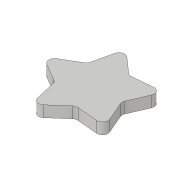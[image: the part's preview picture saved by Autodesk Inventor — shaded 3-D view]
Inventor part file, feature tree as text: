
AUTODESK INVENTOR PART (.ipt)
format: ipt  version: 2019 (Build 230136000, 136)  size: 109,568 bytes
history: native  units: in
note: dims shown in document units (in); Inventor stores cm internally (conversion verified against a paired STEP export)
features: fillet x2, extrude x1, sketch x1
ambient origin geometry x8: Origin, YZ Plane, XZ Plane, XY Plane, X Axis, Y Axis, Z Axis, Center Point
bodies: Body1 (feature_tree)
feature tree (4):
  extrude  "Extrusion2"  Depth=17.7165in
  fillet  "Fillet1"  Radius=19.685in
  fillet  "Fillet2"  Radius=3.937in
  sketch  "Sketch2"  dims[d11=3.937in d16=17.7165in d17=19.685in d18=3.937in d19=0.0in d20=1.9685in d21=1.9685in]
